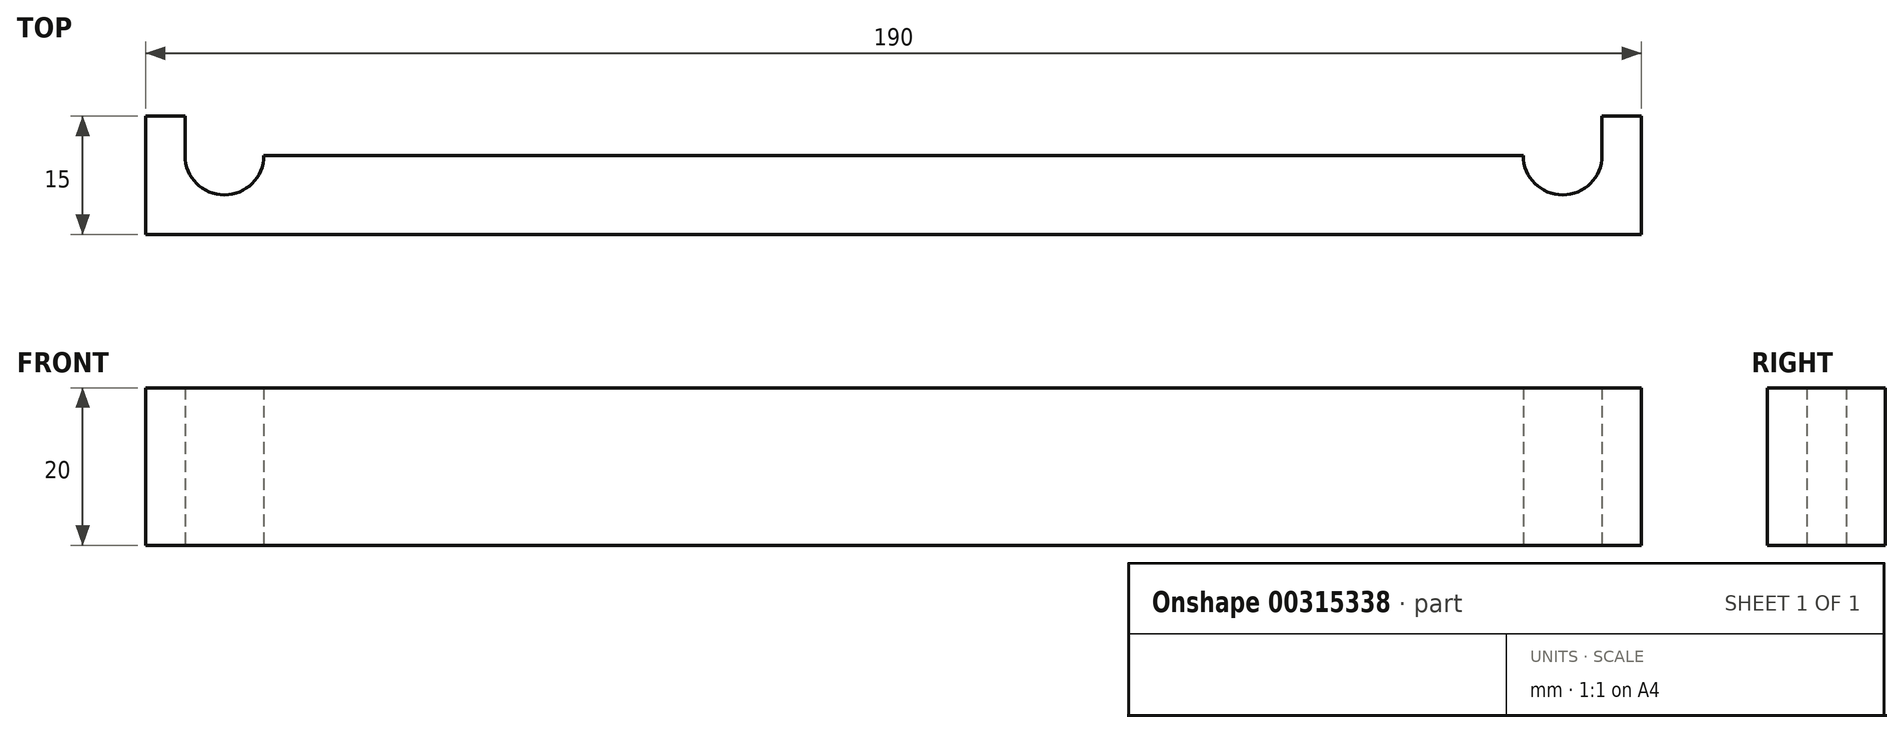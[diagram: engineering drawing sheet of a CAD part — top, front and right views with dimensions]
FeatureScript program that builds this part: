
annotation { "Feature Type Name" : "Feature", "Feature Type Description" : "" }
export const myFeature = defineFeature(function(context is Context, id is Id, definition is map)
    precondition{}
    {
        {
            var Q0;
            Q0=qCreatedBy(makeId("Top.planeOp"),FACE);
            var sketch = newSketch(context, id + "F0", { "sketchPlane" : qUnion([Q0])});
            skCircle(sketch, "E0", {"center": v(-110.82, 12.68) * mm, "radius": 5 * mm});
            skCircle(sketch, "E1", {"center": v(59.18, 12.68) * mm, "radius": 5 * mm});
            skLineSegment(sketch, "E2.bottom", {"start": v(-120.82, 12.68) * mm, "end": v(69.18, 12.68) * mm});
            skLineSegment(sketch, "E2.top", {"start": v(-120.82, 2.68) * mm, "end": v(69.18, 2.68) * mm});
            skLineSegment(sketch, "E2.left", {"start": v(-120.82, 12.68) * mm, "end": v(-120.82, 2.68) * mm});
            skLineSegment(sketch, "E2.right", {"start": v(69.18, 12.68) * mm, "end": v(69.18, 2.68) * mm});
            skSolve(sketch);
        }
        {
            var Q0;
            Q0=makeQuery(id+"F0.imprint","IMPRINT",FACE,{"disambiguationData":[TD([[makeQuery(id+"F0.imprint","IMPRINT",EDGE,{"derivedFrom":sQuery(id+"F0.wireOp",EDGE,"E2.top")}),1.0]])]});
            extrude(context, id + "F1", {"entities" : qUnion([Q0]), "depth" : 20 * mm});
        }
        {
            var Q0;
            {var subQ0=sQuery(id+"F0.wireOp",EDGE,"E2.bottom");Q0=makeQuery(id+"F1.opExtrude","SWEPT_FACE",FACE,{"disambiguationData":[OSD([subQ0]),TDD([makeQuery(id+"F0.imprint","IMPRINT",EDGE,{"disambiguationData":[TD([[makeQuery(id+"F0.imprint","INTERSECT",VERTEX,{"disambiguationData":[OD(1.0)],"derivedFrom":[sQuery(id+"F0.wireOp",EDGE,"E0"),subQ0]}),-1.0]])],"derivedFrom":subQ0})])]});}
            var Q1;
            {var subQ0=sQuery(id+"F0.wireOp",EDGE,"E2.bottom");Q1=makeQuery(id+"F1.opExtrude","SWEPT_FACE",FACE,{"disambiguationData":[OSD([subQ0]),TDD([makeQuery(id+"F0.imprint","IMPRINT",EDGE,{"disambiguationData":[TD([[makeQuery(id+"F0.imprint","INTERSECT",VERTEX,{"derivedFrom":[subQ0,sQuery(id+"F0.wireOp",EDGE,"E2.left")]}),-1.0]])],"derivedFrom":subQ0})])]});}
            var Q2;
            {var subQ0=sQuery(id+"F0.wireOp",EDGE,"E2.bottom");Q2=makeQuery(id+"F1.opExtrude","SWEPT_FACE",FACE,{"disambiguationData":[OSD([subQ0]),TDD([makeQuery(id+"F0.imprint","IMPRINT",EDGE,{"disambiguationData":[TD([[makeQuery(id+"F0.imprint","INTERSECT",VERTEX,{"derivedFrom":[subQ0,sQuery(id+"F0.wireOp",EDGE,"E2.right")]}),1.0]])],"derivedFrom":subQ0})])]});}
            extrude(context, id + "F2", {"entities" : qUnion([Q0, Q1, Q2]), "operationType" : NewBodyOperationType.ADD, "depth" : 5 * mm});
        }
    });
